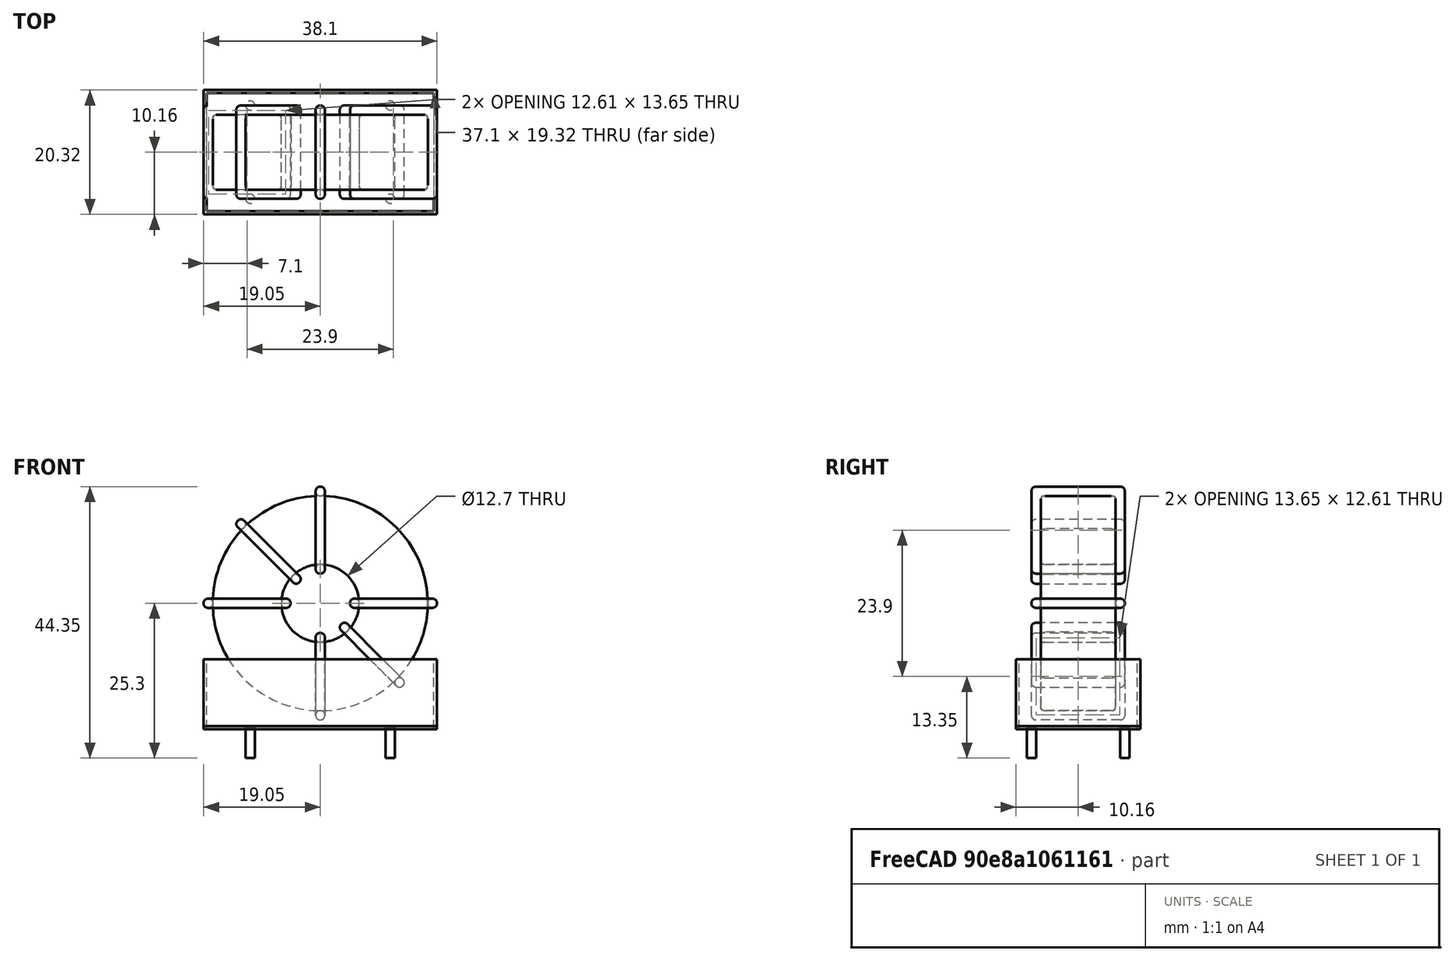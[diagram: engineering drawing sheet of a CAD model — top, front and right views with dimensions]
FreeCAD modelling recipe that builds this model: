
FCSTD DOCUMENT  (FreeCAD 0.16R6703 (Git))
Label: L_CommonModeChoke_Toroid_Vertical_L38.1mm_W20.3mm_Px15.24mm_Py22.86mm_Bourns_8100series
License: All rights reserved
LicenseURL: http://en.wikipedia.org/wiki/All_rights_reserved
objects: Sketcher::SketchObject×8, PartDesign::Pad×8, PartDesign::Fillet×5, Spreadsheet::Sheet×1
note: 29 computed .brp shape members not serialized (recipe doc carries the construction recipe); baked Part::Feature solids carry a one-line shape summary decoded from their .brp

FEATURE [Spreadsheet::Sheet] Spreadsheet  label="dimensions"
  cells = A1=Wx; B1(Wx)=38.09999999999999; C1(WW)=12.7; D1(iWx)=38.09999999999999; A2=Wy; B2(Wy)=15.24; D2(iWy)=20.32; A3=RM; B3(RMx)=15.24; C3(RMy)=22.86; A4=d_wire; B4(d_wire)=1.5; A5=H; B5(H)=31; A6=offsetx; B6(offsetx)=7.619999999999997
FEATURE [Sketcher::SketchObject] Sketch
  Placement = pos=(11.43,-7.62,0) rot=(1,0,0;1.5708rad)
  expr: Placement.Base.x = Spreadsheet.RMy / 2
  expr: Constraints[4] = Spreadsheet.WW / 2
  expr: Placement.Base.y = -Spreadsheet.RMx / 2
  expr: Constraints[0] = Spreadsheet.Wx / 2 - Spreadsheet.d_wire
  expr: Constraints[2] = Spreadsheet.Wx / 2 + Spreadsheet.d_wire + 0.5
  sketch-geometry (2):
    g0: Circle CenterX=0 CenterY=21.05 CenterZ=0 NormalX=0 NormalY=0 NormalZ=1 Radius=17.55
    g1: Circle CenterX=0 CenterY=21.05 CenterZ=0 NormalX=0 NormalY=0 NormalZ=1 Radius=6.35
  constraints (5):
    c: Radius(g0) = 17.55
    c: DistanceX(g-1,g0) = 0
    c: DistanceY(g-1,g0) = 21.05
    c: Coincident(g1,g0)
    c: Radius(g1) = 6.35
FEATURE [PartDesign::Pad] Pad
  Length = 12.24
  Length2 = 100
  Midplane = true
  Placement = pos=(11.43,-7.62,0) rot=(1,0,0;1.5708rad)
  Sketch = -> Sketch
  Type = 0
  expr: Length = Spreadsheet.Wy - 2 * Spreadsheet.d_wire
FEATURE [Sketcher::SketchObject] Sketch001
  Placement = pos=(0,0,0.75) rot=(0,0,1;0rad)
  expr: Constraints[4] = Spreadsheet.RMy
  expr: Constraints[2] = -Spreadsheet.RMx
  expr: Constraints[1] = Spreadsheet.d_wire / 2
  sketch-geometry (4):
    g0: Circle CenterX=0 CenterY=0 CenterZ=0 NormalX=0 NormalY=0 NormalZ=1 Radius=0.75
    g1: Circle CenterX=22.86 CenterY=-15.24 CenterZ=0 NormalX=0 NormalY=0 NormalZ=1 Radius=0.75
    g2: Circle CenterX=0 CenterY=-15.24 CenterZ=0 NormalX=0 NormalY=0 NormalZ=1 Radius=0.75
    g3: Circle CenterX=22.86 CenterY=0 CenterZ=0 NormalX=0 NormalY=0 NormalZ=1 Radius=0.75
  constraints (11):
    c: Equal(g0,g1)
    c: Radius(g0) = 0.75
    c: DistanceY(g-1,g1) = -15.24
    c: Coincident(g0,g-1)
    c: DistanceX(g-1,g1) = 22.86
    c: PointOnObject(g2,g-2)
    c: DistanceY(g-1,g3) = 0
    c: DistanceY(g2,g1) = 0
    c: DistanceX(g3,g1) = 0
    c: Equal(g3,g2)
    c: Equal(g2,g1)
FEATURE [PartDesign::Pad] Pad001
  Length = 5
  Length2 = 0
  Placement = pos=(0,0,0.75) rot=(0,0,1;0rad)
  Reversed = true
  Sketch = -> Sketch001
  Type = 0
FEATURE [PartDesign::Fillet] Fillet
  Base = -> Pad [Edge6,Edge3,Edge2]
  Placement = pos=(11.43,-7.62,0) rot=(1,0,0;1.5708rad)
  Radius = 0.5
FEATURE [Sketcher::SketchObject] Sketch003
  Placement = pos=(11.43,0,21.05) rot=(1,0,0;3.14159rad)
  expr: Placement.Base.x = Spreadsheet.RMy / 2
  expr: Constraints[18] = Spreadsheet.d_wire
  expr: Constraints[16] = Spreadsheet.d_wire
  expr: Constraints[19] = Spreadsheet.d_wire
  expr: Constraints[17] = Spreadsheet.d_wire
  expr: Placement.Base.y = -1 * (Spreadsheet.RMx - Spreadsheet.Wy) / 2
  expr: Constraints[21] = (Spreadsheet.Wx - Spreadsheet.WW) / 2 - Spreadsheet.d_wire
  expr: Constraints[22] = Spreadsheet.Wx / 2 - Spreadsheet.d_wire
  expr: Constraints[43] = Spreadsheet.d_wire
  expr: Constraints[48] = Spreadsheet.Wx - Spreadsheet.d_wire * 2
  expr: Constraints[49] = Spreadsheet.Wy
  expr: Placement.Base.z = Spreadsheet.Wx / 2 + Spreadsheet.d_wire + 0.5
  sketch-geometry (16):
    g0: LineSegment StartX=-4.85 StartY=0 StartZ=0 EndX=-19.05 EndY=0 EndZ=0
    g1: LineSegment StartX=-19.05 StartY=0 StartZ=0 EndX=-19.05 EndY=15.24 EndZ=0
    g2: LineSegment StartX=-19.05 StartY=15.24 StartZ=0 EndX=-4.85 EndY=15.24 EndZ=0
    g3: LineSegment StartX=-4.85 StartY=15.24 StartZ=0 EndX=-4.85 EndY=0 EndZ=0
    g4: LineSegment StartX=-17.55 StartY=13.74 StartZ=0 EndX=-6.35 EndY=13.74 EndZ=0
    g5: LineSegment StartX=-6.35 StartY=13.74 StartZ=0 EndX=-6.35 EndY=1.5 EndZ=0
    g6: LineSegment StartX=-6.35 StartY=1.5 StartZ=0 EndX=-17.55 EndY=1.5 EndZ=0
    g7: LineSegment StartX=-17.55 StartY=1.5 StartZ=0 EndX=-17.55 EndY=13.74 EndZ=0
    g8: LineSegment StartX=4.85 StartY=15.24 StartZ=0 EndX=19.05 EndY=15.24 EndZ=0
    g9: LineSegment StartX=19.05 StartY=15.24 StartZ=0 EndX=19.05 EndY=0 EndZ=0
    g10: LineSegment StartX=19.05 StartY=0 StartZ=0 EndX=4.85 EndY=0 EndZ=0
    g11: LineSegment StartX=4.85 StartY=0 StartZ=0 EndX=4.85 EndY=15.24 EndZ=0
    g12: LineSegment StartX=6.35 StartY=13.74 StartZ=0 EndX=17.55 EndY=13.74 EndZ=0
    g13: LineSegment StartX=17.55 StartY=13.74 StartZ=0 EndX=17.55 EndY=1.5 EndZ=0
    g14: LineSegment StartX=17.55 StartY=1.5 StartZ=0 EndX=6.35 EndY=1.5 EndZ=0
    g15: LineSegment StartX=6.35 StartY=1.5 StartZ=0 EndX=6.35 EndY=13.74 EndZ=0
  constraints (50):
    c: Horizontal(g0)
    c: Coincident(g1,g0)
    c: Vertical(g1)
    c: Coincident(g2,g1)
    c: Horizontal(g2)
    c: Coincident(g3,g2)
    c: Coincident(g3,g0)
    c: Vertical(g3)
    c: Coincident(g4,g5)
    c: Coincident(g5,g6)
    c: Coincident(g6,g7)
    c: Coincident(g7,g4)
    c: Horizontal(g4)
    c: Horizontal(g6)
    c: Vertical(g5)
    c: Vertical(g7)
    c: DistanceX(g1,g4) = 1.5
    c: DistanceY(g4,g1) = 1.5
    c: DistanceX(g5,g0) = 1.5
    c: DistanceY(g0,g5) = 1.5
    c: DistanceY(g-1,g0) = 0
    c: DistanceX(g6,g6) = 11.2
    c: DistanceX(g6,g-1) = 17.55
    c: Coincident(g8,g9)
    c: Coincident(g9,g10)
    c: Coincident(g10,g11)
    c: Coincident(g11,g8)
    c: Horizontal(g8)
    c: Horizontal(g10)
    c: Vertical(g9)
    c: Vertical(g11)
    c: Coincident(g12,g13)
    c: Coincident(g13,g14)
    c: Coincident(g14,g15)
    c: Coincident(g15,g12)
    c: Horizontal(g12)
    c: Horizontal(g14)
    c: Vertical(g13)
    c: Vertical(g15)
    c: DistanceY(g8,g2) = 0
    c: DistanceY(g10,g0) = 0
    c: DistanceY(g14,g5) = 0
    c: DistanceY(g12,g4) = 0
    c: DistanceX(g8,g12) = 1.5
    c: Equal(g8,g2)
    c: Equal(g12,g4)
    c: Equal(g9,g1)
    c: Equal(g13,g7)
    c: DistanceX(g4,g12) = 35.1
    c: DistanceY(g0,g1) = 15.24
FEATURE [PartDesign::Pad] Pad002
  Length = 1.5
  Length2 = 100
  Midplane = true
  Placement = pos=(11.43,0,21.05) rot=(1,0,0;3.14159rad)
  Sketch = -> Sketch003
  Type = 0
  expr: Length = Spreadsheet.d_wire
FEATURE [PartDesign::Fillet] Fillet001
  Base = -> Pad002 [Edge38,Edge41,Edge42,Edge43,Edge29,Edge32,Edge33,Edge34,Edge25,Edge35,Edge36,Edge13,Edge14,Edge15,Edge16,Edge17,Edge18,Edge19,Edge1,Edge2,Edge3,Edge4,Edge5,Edge6,Edge7,Edge37,Edge39,Edge40,Edge20,Edge23,Edge24,Edge21,Edge22,Edge8,Edge9,Edge10,Edge11,Edge12,Edge26,Edge27,+8 more]
  Placement = pos=(11.43,0,21.05) rot=(1,0,0;3.14159rad)
  Radius = 0.705
  expr: Radius = Spreadsheet.d_wire * 0.47
FEATURE [Sketcher::SketchObject] Sketch004
  Placement = pos=(11.43,0,21.05) rot=(0.92388,0,0.382683;3.14159rad)
  expr: Placement.Base.x = Spreadsheet.RMy / 2
  expr: Constraints[18] = Spreadsheet.d_wire
  expr: Constraints[16] = Spreadsheet.d_wire
  expr: Constraints[19] = Spreadsheet.d_wire
  expr: Constraints[17] = Spreadsheet.d_wire
  expr: Placement.Base.y = -1 * (Spreadsheet.RMx - Spreadsheet.Wy) / 2
  expr: Constraints[21] = (Spreadsheet.Wx - Spreadsheet.WW) / 2 - Spreadsheet.d_wire
  expr: Constraints[22] = Spreadsheet.Wx / 2 - Spreadsheet.d_wire
  expr: Constraints[43] = Spreadsheet.d_wire
  expr: Constraints[48] = Spreadsheet.Wx - 2 * Spreadsheet.d_wire
  expr: Constraints[49] = Spreadsheet.Wy
  expr: Placement.Base.z = Spreadsheet.Wx / 2 + Spreadsheet.d_wire + 0.5
  sketch-geometry (16):
    g0: LineSegment StartX=-4.85 StartY=0 StartZ=0 EndX=-19.05 EndY=0 EndZ=0
    g1: LineSegment StartX=-19.05 StartY=0 StartZ=0 EndX=-19.05 EndY=15.24 EndZ=0
    g2: LineSegment StartX=-19.05 StartY=15.24 StartZ=0 EndX=-4.85 EndY=15.24 EndZ=0
    g3: LineSegment StartX=-4.85 StartY=15.24 StartZ=0 EndX=-4.85 EndY=0 EndZ=0
    g4: LineSegment StartX=-17.55 StartY=13.74 StartZ=0 EndX=-6.35 EndY=13.74 EndZ=0
    g5: LineSegment StartX=-6.35 StartY=13.74 StartZ=0 EndX=-6.35 EndY=1.5 EndZ=0
    g6: LineSegment StartX=-6.35 StartY=1.5 StartZ=0 EndX=-17.55 EndY=1.5 EndZ=0
    g7: LineSegment StartX=-17.55 StartY=1.5 StartZ=0 EndX=-17.55 EndY=13.74 EndZ=0
    g8: LineSegment StartX=4.85 StartY=15.24 StartZ=0 EndX=19.05 EndY=15.24 EndZ=0
    g9: LineSegment StartX=19.05 StartY=15.24 StartZ=0 EndX=19.05 EndY=0 EndZ=0
    g10: LineSegment StartX=19.05 StartY=0 StartZ=0 EndX=4.85 EndY=0 EndZ=0
    g11: LineSegment StartX=4.85 StartY=0 StartZ=0 EndX=4.85 EndY=15.24 EndZ=0
    g12: LineSegment StartX=6.35 StartY=13.74 StartZ=0 EndX=17.55 EndY=13.74 EndZ=0
    g13: LineSegment StartX=17.55 StartY=13.74 StartZ=0 EndX=17.55 EndY=1.5 EndZ=0
    g14: LineSegment StartX=17.55 StartY=1.5 StartZ=0 EndX=6.35 EndY=1.5 EndZ=0
    g15: LineSegment StartX=6.35 StartY=1.5 StartZ=0 EndX=6.35 EndY=13.74 EndZ=0
  constraints (50):
    c: Horizontal(g0)
    c: Coincident(g1,g0)
    c: Vertical(g1)
    c: Coincident(g2,g1)
    c: Horizontal(g2)
    c: Coincident(g3,g2)
    c: Coincident(g3,g0)
    c: Vertical(g3)
    c: Coincident(g4,g5)
    c: Coincident(g5,g6)
    c: Coincident(g6,g7)
    c: Coincident(g7,g4)
    c: Horizontal(g4)
    c: Horizontal(g6)
    c: Vertical(g5)
    c: Vertical(g7)
    c: DistanceX(g1,g4) = 1.5
    c: DistanceY(g4,g1) = 1.5
    c: DistanceX(g5,g0) = 1.5
    c: DistanceY(g0,g5) = 1.5
    c: DistanceY(g-1,g0) = 0
    c: DistanceX(g6,g6) = 11.2
    c: DistanceX(g6,g-1) = 17.55
    c: Coincident(g8,g9)
    c: Coincident(g9,g10)
    c: Coincident(g10,g11)
    c: Coincident(g11,g8)
    c: Horizontal(g8)
    c: Horizontal(g10)
    c: Vertical(g9)
    c: Vertical(g11)
    c: Coincident(g12,g13)
    c: Coincident(g13,g14)
    c: Coincident(g14,g15)
    c: Coincident(g15,g12)
    c: Horizontal(g12)
    c: Horizontal(g14)
    c: Vertical(g13)
    c: Vertical(g15)
    c: DistanceY(g8,g2) = 0
    c: DistanceY(g10,g0) = 0
    c: DistanceY(g14,g5) = 0
    c: DistanceY(g12,g4) = 0
    c: DistanceX(g8,g12) = 1.5
    c: Equal(g8,g2)
    c: Equal(g12,g4)
    c: Equal(g9,g1)
    c: Equal(g13,g7)
    c: DistanceX(g4,g12) = 35.1
    c: DistanceY(g0,g1) = 15.24
FEATURE [PartDesign::Pad] Pad003
  Length = 1.5
  Length2 = 100
  Midplane = true
  Placement = pos=(11.43,0,21.05) rot=(0.92388,0,0.382683;3.14159rad)
  Sketch = -> Sketch004
  Type = 0
  expr: Length = Spreadsheet.d_wire
FEATURE [PartDesign::Fillet] Fillet002
  Base = -> Pad003 [Edge38,Edge41,Edge42,Edge43,Edge29,Edge32,Edge33,Edge34,Edge25,Edge35,Edge36,Edge13,Edge14,Edge15,Edge16,Edge17,Edge18,Edge19,Edge1,Edge2,Edge3,Edge4,Edge5,Edge6,Edge7,Edge37,Edge39,Edge40,Edge20,Edge23,Edge24,Edge21,Edge22,Edge8,Edge9,Edge10,Edge11,Edge12,Edge26,Edge27,+8 more]
  Placement = pos=(11.43,0,21.05) rot=(0.92388,0,0.382683;3.14159rad)
  Radius = 0.705
  expr: Radius = Spreadsheet.d_wire * 0.47
FEATURE [Sketcher::SketchObject] Sketch005
  Placement = pos=(11.43,0,21.05) rot=(0.92388,0,-0.382683;3.14159rad)
  expr: Placement.Base.x = Spreadsheet.RMy / 2
  expr: Constraints[18] = Spreadsheet.d_wire
  expr: Constraints[16] = Spreadsheet.d_wire
  expr: Constraints[19] = Spreadsheet.d_wire
  expr: Constraints[17] = Spreadsheet.d_wire
  expr: Placement.Base.y = -1 * (Spreadsheet.RMx - Spreadsheet.Wy) / 2
  expr: Constraints[21] = (Spreadsheet.Wx - Spreadsheet.WW) / 2 - Spreadsheet.d_wire
  expr: Constraints[22] = Spreadsheet.Wx / 2 - Spreadsheet.d_wire
  expr: Constraints[43] = Spreadsheet.d_wire
  expr: Constraints[48] = Spreadsheet.Wx - 2 * Spreadsheet.d_wire
  expr: Constraints[49] = Spreadsheet.Wy
  expr: Placement.Base.z = Spreadsheet.Wx / 2 + Spreadsheet.d_wire + 0.5
  sketch-geometry (16):
    g0: LineSegment StartX=-4.85 StartY=0 StartZ=0 EndX=-19.05 EndY=0 EndZ=0
    g1: LineSegment StartX=-19.05 StartY=0 StartZ=0 EndX=-19.05 EndY=15.24 EndZ=0
    g2: LineSegment StartX=-19.05 StartY=15.24 StartZ=0 EndX=-4.85 EndY=15.24 EndZ=0
    g3: LineSegment StartX=-4.85 StartY=15.24 StartZ=0 EndX=-4.85 EndY=0 EndZ=0
    g4: LineSegment StartX=-17.55 StartY=13.74 StartZ=0 EndX=-6.35 EndY=13.74 EndZ=0
    g5: LineSegment StartX=-6.35 StartY=13.74 StartZ=0 EndX=-6.35 EndY=1.5 EndZ=0
    g6: LineSegment StartX=-6.35 StartY=1.5 StartZ=0 EndX=-17.55 EndY=1.5 EndZ=0
    g7: LineSegment StartX=-17.55 StartY=1.5 StartZ=0 EndX=-17.55 EndY=13.74 EndZ=0
    g8: LineSegment StartX=4.85 StartY=15.24 StartZ=0 EndX=19.05 EndY=15.24 EndZ=0
    g9: LineSegment StartX=19.05 StartY=15.24 StartZ=0 EndX=19.05 EndY=0 EndZ=0
    g10: LineSegment StartX=19.05 StartY=0 StartZ=0 EndX=4.85 EndY=0 EndZ=0
    g11: LineSegment StartX=4.85 StartY=0 StartZ=0 EndX=4.85 EndY=15.24 EndZ=0
    g12: LineSegment StartX=6.35 StartY=13.74 StartZ=0 EndX=17.55 EndY=13.74 EndZ=0
    g13: LineSegment StartX=17.55 StartY=13.74 StartZ=0 EndX=17.55 EndY=1.5 EndZ=0
    g14: LineSegment StartX=17.55 StartY=1.5 StartZ=0 EndX=6.35 EndY=1.5 EndZ=0
    g15: LineSegment StartX=6.35 StartY=1.5 StartZ=0 EndX=6.35 EndY=13.74 EndZ=0
  constraints (50):
    c: Horizontal(g0)
    c: Coincident(g1,g0)
    c: Vertical(g1)
    c: Coincident(g2,g1)
    c: Horizontal(g2)
    c: Coincident(g3,g2)
    c: Coincident(g3,g0)
    c: Vertical(g3)
    c: Coincident(g4,g5)
    c: Coincident(g5,g6)
    c: Coincident(g6,g7)
    c: Coincident(g7,g4)
    c: Horizontal(g4)
    c: Horizontal(g6)
    c: Vertical(g5)
    c: Vertical(g7)
    c: DistanceX(g1,g4) = 1.5
    c: DistanceY(g4,g1) = 1.5
    c: DistanceX(g5,g0) = 1.5
    c: DistanceY(g0,g5) = 1.5
    c: DistanceY(g-1,g0) = 0
    c: DistanceX(g6,g6) = 11.2
    c: DistanceX(g6,g-1) = 17.55
    c: Coincident(g8,g9)
    c: Coincident(g9,g10)
    c: Coincident(g10,g11)
    c: Coincident(g11,g8)
    c: Horizontal(g8)
    c: Horizontal(g10)
    c: Vertical(g9)
    c: Vertical(g11)
    c: Coincident(g12,g13)
    c: Coincident(g13,g14)
    c: Coincident(g14,g15)
    c: Coincident(g15,g12)
    c: Horizontal(g12)
    c: Horizontal(g14)
    c: Vertical(g13)
    c: Vertical(g15)
    c: DistanceY(g8,g2) = 0
    c: DistanceY(g10,g0) = 0
    c: DistanceY(g14,g5) = 0
    c: DistanceY(g12,g4) = 0
    c: DistanceX(g8,g12) = 1.5
    c: Equal(g8,g2)
    c: Equal(g12,g4)
    c: Equal(g9,g1)
    c: Equal(g13,g7)
    c: DistanceX(g4,g12) = 35.1
    c: DistanceY(g0,g1) = 15.24
FEATURE [PartDesign::Pad] Pad004
  Length = 1.5
  Length2 = 100
  Midplane = true
  Placement = pos=(11.43,0,21.05) rot=(0.92388,0,-0.382683;3.14159rad)
  Sketch = -> Sketch005
  Type = 0
  expr: Length = Spreadsheet.d_wire
FEATURE [PartDesign::Fillet] Fillet003
  Base = -> Pad004 [Edge38,Edge41,Edge42,Edge43,Edge29,Edge32,Edge33,Edge34,Edge25,Edge35,Edge36,Edge13,Edge14,Edge15,Edge16,Edge17,Edge18,Edge19,Edge1,Edge2,Edge3,Edge4,Edge5,Edge6,Edge7,Edge37,Edge39,Edge40,Edge20,Edge23,Edge24,Edge21,Edge22,Edge8,Edge9,Edge10,Edge11,Edge12,Edge26,Edge27,+8 more]
  Placement = pos=(11.43,0,21.05) rot=(0.92388,0,-0.382683;3.14159rad)
  Radius = 0.705
  expr: Radius = Spreadsheet.d_wire * 0.47
FEATURE [Sketcher::SketchObject] Sketch006
  Placement = pos=(11.43,0,21.05) rot=(0.707107,0,0.707107;3.14159rad)
  expr: Placement.Base.x = Spreadsheet.RMy / 2
  expr: Constraints[18] = Spreadsheet.d_wire
  expr: Constraints[16] = Spreadsheet.d_wire
  expr: Constraints[19] = Spreadsheet.d_wire
  expr: Constraints[17] = Spreadsheet.d_wire
  expr: Placement.Base.y = -1 * (Spreadsheet.RMx - Spreadsheet.Wy) / 2
  expr: Constraints[21] = (Spreadsheet.Wx - Spreadsheet.WW) / 2 - Spreadsheet.d_wire
  expr: Constraints[22] = Spreadsheet.Wx / 2 - Spreadsheet.d_wire
  expr: Constraints[43] = Spreadsheet.d_wire
  expr: Constraints[48] = Spreadsheet.Wx - Spreadsheet.d_wire * 2
  expr: Constraints[49] = Spreadsheet.Wy
  expr: Placement.Base.z = Spreadsheet.Wx / 2 + Spreadsheet.d_wire + 0.5
  sketch-geometry (16):
    g0: LineSegment StartX=-4.85 StartY=0 StartZ=0 EndX=-19.05 EndY=0 EndZ=0
    g1: LineSegment StartX=-19.05 StartY=0 StartZ=0 EndX=-19.05 EndY=15.24 EndZ=0
    g2: LineSegment StartX=-19.05 StartY=15.24 StartZ=0 EndX=-4.85 EndY=15.24 EndZ=0
    g3: LineSegment StartX=-4.85 StartY=15.24 StartZ=0 EndX=-4.85 EndY=0 EndZ=0
    g4: LineSegment StartX=-17.55 StartY=13.74 StartZ=0 EndX=-6.35 EndY=13.74 EndZ=0
    g5: LineSegment StartX=-6.35 StartY=13.74 StartZ=0 EndX=-6.35 EndY=1.5 EndZ=0
    g6: LineSegment StartX=-6.35 StartY=1.5 StartZ=0 EndX=-17.55 EndY=1.5 EndZ=0
    g7: LineSegment StartX=-17.55 StartY=1.5 StartZ=0 EndX=-17.55 EndY=13.74 EndZ=0
    g8: LineSegment StartX=4.85 StartY=15.24 StartZ=0 EndX=19.05 EndY=15.24 EndZ=0
    g9: LineSegment StartX=19.05 StartY=15.24 StartZ=0 EndX=19.05 EndY=0 EndZ=0
    g10: LineSegment StartX=19.05 StartY=0 StartZ=0 EndX=4.85 EndY=0 EndZ=0
    g11: LineSegment StartX=4.85 StartY=0 StartZ=0 EndX=4.85 EndY=15.24 EndZ=0
    g12: LineSegment StartX=6.35 StartY=13.74 StartZ=0 EndX=17.55 EndY=13.74 EndZ=0
    g13: LineSegment StartX=17.55 StartY=13.74 StartZ=0 EndX=17.55 EndY=1.5 EndZ=0
    g14: LineSegment StartX=17.55 StartY=1.5 StartZ=0 EndX=6.35 EndY=1.5 EndZ=0
    g15: LineSegment StartX=6.35 StartY=1.5 StartZ=0 EndX=6.35 EndY=13.74 EndZ=0
  constraints (50):
    c: Horizontal(g0)
    c: Coincident(g1,g0)
    c: Vertical(g1)
    c: Coincident(g2,g1)
    c: Horizontal(g2)
    c: Coincident(g3,g2)
    c: Coincident(g3,g0)
    c: Vertical(g3)
    c: Coincident(g4,g5)
    c: Coincident(g5,g6)
    c: Coincident(g6,g7)
    c: Coincident(g7,g4)
    c: Horizontal(g4)
    c: Horizontal(g6)
    c: Vertical(g5)
    c: Vertical(g7)
    c: DistanceX(g1,g4) = 1.5
    c: DistanceY(g4,g1) = 1.5
    c: DistanceX(g5,g0) = 1.5
    c: DistanceY(g0,g5) = 1.5
    c: DistanceY(g-1,g0) = 0
    c: DistanceX(g6,g6) = 11.2
    c: DistanceX(g6,g-1) = 17.55
    c: Coincident(g8,g9)
    c: Coincident(g9,g10)
    c: Coincident(g10,g11)
    c: Coincident(g11,g8)
    c: Horizontal(g8)
    c: Horizontal(g10)
    c: Vertical(g9)
    c: Vertical(g11)
    c: Coincident(g12,g13)
    c: Coincident(g13,g14)
    c: Coincident(g14,g15)
    c: Coincident(g15,g12)
    c: Horizontal(g12)
    c: Horizontal(g14)
    c: Vertical(g13)
    c: Vertical(g15)
    c: DistanceY(g8,g2) = 0
    c: DistanceY(g10,g0) = 0
    c: DistanceY(g14,g5) = 0
    c: DistanceY(g12,g4) = 0
    c: DistanceX(g8,g12) = 1.5
    c: Equal(g8,g2)
    c: Equal(g12,g4)
    c: Equal(g9,g1)
    c: Equal(g13,g7)
    c: DistanceX(g4,g12) = 35.1
    c: DistanceY(g0,g1) = 15.24
FEATURE [PartDesign::Pad] Pad005
  Length = 1.5
  Length2 = 100
  Midplane = true
  Placement = pos=(11.43,0,21.05) rot=(0.707107,0,0.707107;3.14159rad)
  Sketch = -> Sketch006
  Type = 0
  expr: Length = Spreadsheet.d_wire
FEATURE [PartDesign::Fillet] Fillet004
  Base = -> Pad005 [Edge38,Edge41,Edge42,Edge43,Edge29,Edge32,Edge33,Edge34,Edge25,Edge35,Edge36,Edge13,Edge14,Edge15,Edge16,Edge17,Edge18,Edge19,Edge1,Edge2,Edge3,Edge4,Edge5,Edge6,Edge7,Edge37,Edge39,Edge40,Edge20,Edge23,Edge24,Edge21,Edge22,Edge8,Edge9,Edge10,Edge11,Edge12,Edge26,Edge27,+8 more]
  Placement = pos=(11.43,0,21.05) rot=(0.707107,0,0.707107;3.14159rad)
  Radius = 0.705
  expr: Radius = Spreadsheet.d_wire * 0.47
FEATURE [Sketcher::SketchObject] Sketch007
  Placement = pos=(11.43,0,0.5) rot=(0,0,1;0rad)
  expr: Placement.Base.x = Spreadsheet.RMy / 2
  expr: Placement.Base.z = 0.5
  expr: Constraints[11] = Spreadsheet.iWx / 2
  expr: Constraints[10] = (Spreadsheet.iWy - Spreadsheet.RMx) / 2
  expr: Constraints[9] = Spreadsheet.iWy
  expr: Constraints[8] = Spreadsheet.iWx
  sketch-geometry (4):
    g0: LineSegment StartX=-19.05 StartY=2.54 StartZ=0 EndX=19.05 EndY=2.54 EndZ=0
    g1: LineSegment StartX=19.05 StartY=2.54 StartZ=0 EndX=19.05 EndY=-17.78 EndZ=0
    g2: LineSegment StartX=19.05 StartY=-17.78 StartZ=0 EndX=-19.05 EndY=-17.78 EndZ=0
    g3: LineSegment StartX=-19.05 StartY=-17.78 StartZ=0 EndX=-19.05 EndY=2.54 EndZ=0
  constraints (12):
    c: Coincident(g0,g1)
    c: Coincident(g1,g2)
    c: Coincident(g2,g3)
    c: Coincident(g3,g0)
    c: Horizontal(g0)
    c: Horizontal(g2)
    c: Vertical(g1)
    c: Vertical(g3)
    c: DistanceX(g0,g0) = 38.1
    c: DistanceY(g3,g3) = 20.32
    c: DistanceY(g-1,g0) = 2.54
    c: DistanceX(g0,g-1) = 19.05
FEATURE [PartDesign::Pad] Pad006
  Length = 0.5
  Length2 = 100
  Placement = pos=(11.43,0,0.5) rot=(0,0,1;0rad)
  Sketch = -> Sketch007
  Type = 0
FEATURE [Sketcher::SketchObject] Sketch008
  Placement = pos=(11.43,0,0.5) rot=(0,0,1;0rad)
  expr: Placement.Base.x = Spreadsheet.RMy / 2
  expr: Constraints[8] = Spreadsheet.iWx
  expr: Constraints[9] = Spreadsheet.iWy
  expr: Constraints[10] = (Spreadsheet.iWy - Spreadsheet.RMx) / 2
  expr: Placement.Base.z = 0.5
  expr: Constraints[21] = 0.5
  expr: Constraints[11] = Spreadsheet.iWx / 2
  sketch-geometry (8):
    g0: LineSegment StartX=-19.05 StartY=2.54 StartZ=0 EndX=19.05 EndY=2.54 EndZ=0
    g1: LineSegment StartX=19.05 StartY=2.54 StartZ=0 EndX=19.05 EndY=-17.78 EndZ=0
    g2: LineSegment StartX=19.05 StartY=-17.78 StartZ=0 EndX=-19.05 EndY=-17.78 EndZ=0
    g3: LineSegment StartX=-19.05 StartY=-17.78 StartZ=0 EndX=-19.05 EndY=2.54 EndZ=0
    g4: LineSegment StartX=-18.55 StartY=2.04 StartZ=0 EndX=18.55 EndY=2.04 EndZ=0
    g5: LineSegment StartX=18.55 StartY=2.04 StartZ=0 EndX=18.55 EndY=-17.28 EndZ=0
    g6: LineSegment StartX=18.55 StartY=-17.28 StartZ=0 EndX=-18.55 EndY=-17.28 EndZ=0
    g7: LineSegment StartX=-18.55 StartY=-17.28 StartZ=0 EndX=-18.55 EndY=2.04 EndZ=0
  constraints (24):
    c: Coincident(g0,g1)
    c: Coincident(g1,g2)
    c: Coincident(g2,g3)
    c: Coincident(g3,g0)
    c: Horizontal(g0)
    c: Horizontal(g2)
    c: Vertical(g1)
    c: Vertical(g3)
    c: DistanceX(g0,g0) = 38.1
    c: DistanceY(g3,g3) = 20.32
    c: DistanceY(g-1,g0) = 2.54
    c: DistanceX(g0,g-1) = 19.05
    c: Coincident(g4,g5)
    c: Coincident(g5,g6)
    c: Coincident(g6,g7)
    c: Coincident(g7,g4)
    c: Horizontal(g4)
    c: Horizontal(g6)
    c: Vertical(g5)
    c: Vertical(g7)
    c: DistanceX(g5,g1) = 0.5
    c: DistanceY(g1,g5) = 0.5
    c: DistanceX(g0,g4) = 0.5
    c: DistanceY(g4,g0) = 0.5
FEATURE [PartDesign::Pad] Pad007
  Length = 11.43
  Length2 = 100
  Placement = pos=(11.43,0,0.5) rot=(0,0,1;0rad)
  Sketch = -> Sketch008
  Type = 0
  expr: Length = Spreadsheet.Wx * 0.3
